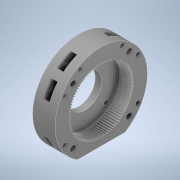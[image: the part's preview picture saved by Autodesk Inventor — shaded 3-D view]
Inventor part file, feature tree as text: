
AUTODESK INVENTOR PART (.ipt)
format: ipt  version: 2022 (Build 260153000, 153)  size: 726,016 bytes
history: mixed  units: in
note: dims shown in document units (in); Inventor stores cm internally (conversion verified against a paired STEP export)
features: sketch x4, extrude x3, plane x1, hole x1, other x1, imported_body x1
ambient origin geometry x8: Origin, YZ Plane, XZ Plane, XY Plane, X Axis, Y Axis, Z Axis, Center Point
bodies: Solid1 (imported_parasolid)
feature tree (11):
  extrude  "Extrusion1"  Depth=0.3937in TaperAngle=0.0deg
  extrude  "Extrusion2"  Depth=0.3937in TaperAngle=0.0deg
  plane  "Work Plane1"
  extrude  "Extrusion3"  Depth=0.1772in TaperAngle=0.0deg
  hole  "Hole1"  [1 undecoded]
  sketch  "Sketch2"  dims[d1=1.5748in d3=360.0deg d5=0.3937in d6=0.0in]
  sketch  "Sketch3"  dims[d7=1.5748in d9=360.0deg d11=0.3937in d12=0.0in]
  sketch  "Sketch4"  dims[d19=1.5748in d21=360.0deg d23=0.1772in d24=0.0in]
  sketch  "Sketch5"  dims[d25=0.1378in d26=0.2362in d27=0.1969in d28=0.1181in d29=90.0deg d30=0.315in d31=0.8108in d8=0.0344in]
  other  "96_Teeth_Gear.STEP"
  imported_body  NMx_Import_Brep_tag  [imported B-rep: ~453 faces, bbox_mm=[17.0, 62.865012, 65.730025]]
note: 1 required parameter value undecoded (feature->parameter linkage not recoverable at this tier; creation-order binding heuristic only, values carry confidence <= 0.55)
